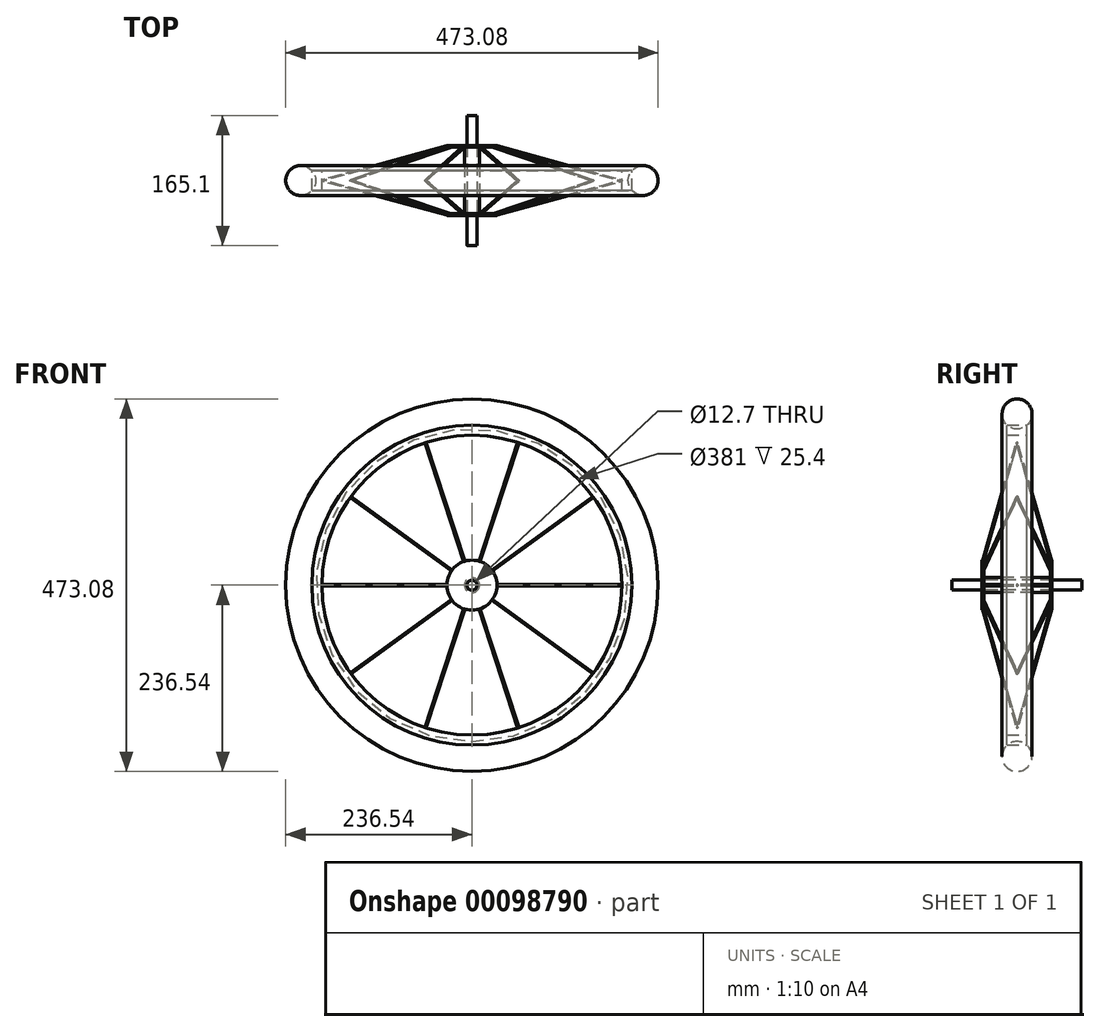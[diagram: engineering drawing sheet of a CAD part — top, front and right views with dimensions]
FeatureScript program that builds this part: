
annotation { "Feature Type Name" : "Feature", "Feature Type Description" : "" }
export const myFeature = defineFeature(function(context is Context, id is Id, definition is map)
    precondition{}
    {
        {
            var Q0;
            Q0=qCreatedBy(makeId("Front.planeOp"),FACE);
            var sketch = newSketch(context, id + "F0", { "sketchPlane" : qUnion([Q0])});
            skCircle(sketch, "E0", {"center": v(0, 0) * mm, "radius": 203.2 * mm});
            skCircle(sketch, "E1", {"center": v(0, 0) * mm, "radius": 190.5 * mm});
            skCircle(sketch, "E2.cCircle", {"center": v(0, 0) * mm, "radius": 163.56 * mm, "construction": true});
            skLineSegment(sketch, "E2.0", {"start": v(163.56, 43.83) * mm, "end": v(163.56, -43.83) * mm});
            skLineSegment(sketch, "E2.1", {"start": v(163.56, -43.83) * mm, "end": v(119.74, -119.74) * mm});
            skLineSegment(sketch, "E2.2", {"start": v(119.74, -119.74) * mm, "end": v(43.83, -163.56) * mm});
            skLineSegment(sketch, "E2.3", {"start": v(43.83, -163.56) * mm, "end": v(-43.83, -163.56) * mm});
            skLineSegment(sketch, "E2.4", {"start": v(-43.83, -163.56) * mm, "end": v(-119.74, -119.74) * mm});
            skLineSegment(sketch, "E2.5", {"start": v(-119.74, -119.74) * mm, "end": v(-163.56, -43.83) * mm});
            skLineSegment(sketch, "E2.6", {"start": v(-163.56, -43.83) * mm, "end": v(-163.56, 43.83) * mm});
            skLineSegment(sketch, "E2.7", {"start": v(-163.56, 43.83) * mm, "end": v(-119.74, 119.74) * mm});
            skLineSegment(sketch, "E2.8", {"start": v(-119.74, 119.74) * mm, "end": v(-43.83, 163.56) * mm});
            skLineSegment(sketch, "E2.9", {"start": v(-43.83, 163.56) * mm, "end": v(43.83, 163.56) * mm});
            skLineSegment(sketch, "E2.10", {"start": v(43.83, 163.56) * mm, "end": v(119.74, 119.74) * mm});
            skLineSegment(sketch, "E2.11", {"start": v(119.74, 119.74) * mm, "end": v(163.56, 43.83) * mm});
            skPoint(sketch, "E2.0.midPoint", {"position": v(163.56, 0) * mm});
            skLineSegment(sketch, "E3", {"start": v(163.56, 43.83) * mm, "end": v(-163.56, -43.83) * mm});
            skLineSegment(sketch, "E4", {"start": v(119.74, -119.74) * mm, "end": v(-119.74, 119.74) * mm});
            skLineSegment(sketch, "E5", {"start": v(-43.83, -163.56) * mm, "end": v(43.83, 163.56) * mm});
            skLineSegment(sketch, "E6", {"start": v(-119.74, -119.74) * mm, "end": v(119.74, 119.74) * mm});
            skLineSegment(sketch, "E7", {"start": v(43.83, -163.56) * mm, "end": v(-43.83, 163.56) * mm});
            skLineSegment(sketch, "E8", {"start": v(163.56, -43.83) * mm, "end": v(-163.56, 43.83) * mm});
            skSolve(sketch);
        }
        {
            var Q0;
            Q0 = qSketchRegion(id + "F0", true);
            extrude(context, id + "F1", {"entities" : qUnion([Q0]), "depth" : 25.4 * mm, "symmetric" : true});
        }
        {
            var Q0;
            Q0=qCreatedBy(makeId("Right.planeOp"),FACE);
            var sketch = newSketch(context, id + "F2", { "sketchPlane" : qUnion([Q0])});
            skLineSegment(sketch, "E9", {"start": v(-44.45, 6.35) * mm, "end": v(-44.45, 31.75) * mm});
            skLineSegment(sketch, "E10", {"start": v(-44.45, 31.75) * mm, "end": v(-42.16, 31.75) * mm});
            skLineSegment(sketch, "E11", {"start": v(-42.16, 31.75) * mm, "end": v(-42.16, 9.53) * mm});
            skLineSegment(sketch, "E12", {"start": v(-44.45, 6.35) * mm, "end": v(44.45, 6.35) * mm});
            skLineSegment(sketch, "E13", {"start": v(42.16, 9.53) * mm, "end": v(42.16, 31.75) * mm});
            skLineSegment(sketch, "E14", {"start": v(42.16, 31.75) * mm, "end": v(44.45, 31.75) * mm});
            skLineSegment(sketch, "E15", {"start": v(44.45, 31.75) * mm, "end": v(44.45, 6.35) * mm});
            skPoint(sketch, "E16.orphan", {"position": v(-44.45, 0) * mm});
            skPoint(sketch, "E17.orphan", {"position": v(44.45, 0) * mm});
            skLineSegment(sketch, "E18.trimOffspring", {"start": v(-42.16, 9.53) * mm, "end": v(42.16, 9.53) * mm});
            skSolve(sketch);
        }
        {
            var Q0;
            Q0=makeQuery(id+"F2.imprint","IMPRINT",FACE,{"disambiguationData":[TD([[makeQuery(id+"F2.imprint","IMPRINT",EDGE,{"derivedFrom":sQuery(id+"F2.wireOp",EDGE,"E9")}),-1.0]])]});
            var Q1;
            Q1=makeQuery(id+"F1.opExtrude","CAP_EDGE",EDGE,{"disambiguationData":[OSD([sQuery(id+"F0.wireOp",EDGE,"E1")])],"isStart":false});
            sweep(context, id + "F3", {"profiles" : qUnion([Q0]), "path" : qUnion([Q1])});
        }
        {
            var Q0;
            Q0=qCreatedBy(makeId("Top.planeOp"),FACE);
            var sketch = newSketch(context, id + "F4", { "sketchPlane" : qUnion([Q0])});
            skLineSegment(sketch, "E19", {"start": v(31.75, 42.5) * mm, "end": v(190.5, -0.76) * mm});
            skLineSegment(sketch, "E20", {"start": v(31.75, 44.09) * mm, "end": v(190.5, 0.82) * mm});
            skLineSegment(sketch, "E21", {"start": v(31.75, 42.5) * mm, "end": v(31.75, 44.09) * mm});
            skLineSegment(sketch, "E22", {"start": v(190.5, -0.76) * mm, "end": v(190.5, 0.82) * mm});
            skSolve(sketch);
        }
        {
            var Q0;
            Q0=makeQuery(id+"F4.imprint","IMPRINT",FACE,{"disambiguationData":[TD([[makeQuery(id+"F4.imprint","IMPRINT",EDGE,{"derivedFrom":sQuery(id+"F4.wireOp",EDGE,"E19")}),1.0]])]});
            extrude(context, id + "F5", {"entities" : qUnion([Q0]), "depth" : 1.52 * mm, "symmetric" : true});
        }
        {
            var Q0;
            Q0=qCreatedBy(makeId("Front.planeOp"),FACE);
            var sketch = newSketch(context, id + "F6", { "sketchPlane" : qUnion([Q0])});
            skPoint(sketch, "E23.0.midPoint", {"position": v(0, 148.93) * mm});
            skLineSegment(sketch, "E24", {"start": v(0, 0) * mm, "end": v(126.69, 92.05) * mm});
            skLineSegment(sketch, "E25", {"start": v(0, 0) * mm, "end": v(48.4, 148.93) * mm});
            skLineSegment(sketch, "E26", {"start": v(0, 0) * mm, "end": v(-48.4, 148.93) * mm});
            skLineSegment(sketch, "E27", {"start": v(0, 0) * mm, "end": v(-126.69, 92.05) * mm});
            skSolve(sketch);
        }
        {
            var Q0;
            Q0=sQuery(id+"F6.wireOp",EDGE,"E24");
            cPlane(context, id + "F7", {"entities" : qUnion([Q0]), "cplaneType" : CPlaneType.LINE_ANGLE, "offset" : 152.4 * mm, "angle" : 90 * degree, "width" : 152.4 * mm, "height" : 152.4 * mm});
        }
        {
            var Q0;
            Q0=sQuery(id+"F6.wireOp",EDGE,"E25");
            cPlane(context, id + "F8", {"entities" : qUnion([Q0]), "cplaneType" : CPlaneType.LINE_ANGLE, "offset" : 152.4 * mm, "angle" : 0 * degree, "width" : 152.4 * mm, "height" : 152.4 * mm});
        }
        {
            var Q0;
            Q0=sQuery(id+"F6.wireOp",EDGE,"E27");
            cPlane(context, id + "F9", {"entities" : qUnion([Q0]), "cplaneType" : CPlaneType.LINE_ANGLE, "offset" : 152.4 * mm, "angle" : 90 * degree, "width" : 152.4 * mm, "height" : 152.4 * mm});
        }
        {
            var Q0;
            Q0=makeQuery(id+"F5.opExtrude","SWEPT_BODY",BODY,{"disambiguationData":[OSD([sQuery(id+"F4.wireOp",EDGE,"E19"),sQuery(id+"F4.wireOp",EDGE,"E20"),sQuery(id+"F4.wireOp",EDGE,"E21"),sQuery(id+"F4.wireOp",EDGE,"E22")])]});
            var Q1;
            Q1=qCreatedBy(id+"F7.planeOp",FACE);
            mirror(context, id + "F10", {"entities" : qUnion([Q0]), "mirrorPlane" : qUnion([Q1])});
        }
        {
            var Q0;
            Q0=makeQuery(id+"F10.opPattern","COPY",BODY,{"derivedFrom":makeQuery(id+"F5.opExtrude","SWEPT_BODY",BODY,{"disambiguationData":[OSD([sQuery(id+"F4.wireOp",EDGE,"E19"),sQuery(id+"F4.wireOp",EDGE,"E20"),sQuery(id+"F4.wireOp",EDGE,"E21"),sQuery(id+"F4.wireOp",EDGE,"E22")])]}),"instanceName":"1"});
            var Q1;
            Q1=qCreatedBy(id+"F9.planeOp",FACE);
            mirror(context, id + "F11", {"entities" : qUnion([Q0]), "mirrorPlane" : qUnion([Q1])});
        }
        {
            var Q0;
            Q0=makeQuery(id+"F5.opExtrude","SWEPT_BODY",BODY,{"disambiguationData":[OSD([sQuery(id+"F4.wireOp",EDGE,"E19"),sQuery(id+"F4.wireOp",EDGE,"E20"),sQuery(id+"F4.wireOp",EDGE,"E21"),sQuery(id+"F4.wireOp",EDGE,"E22")])]});
            var Q1;
            Q1=qCreatedBy(id+"F8.planeOp",FACE);
            mirror(context, id + "F12", {"entities" : qUnion([Q0]), "mirrorPlane" : qUnion([Q1])});
        }
        {
            var Q0;
            Q0=makeQuery(id+"F5.opExtrude","SWEPT_BODY",BODY,{"disambiguationData":[OSD([sQuery(id+"F4.wireOp",EDGE,"E19"),sQuery(id+"F4.wireOp",EDGE,"E20"),sQuery(id+"F4.wireOp",EDGE,"E21"),sQuery(id+"F4.wireOp",EDGE,"E22")])]});
            var Q1;
            Q1=qCreatedBy(makeId("Right.planeOp"),FACE);
            mirror(context, id + "F13", {"entities" : qUnion([Q0]), "mirrorPlane" : qUnion([Q1])});
        }
        {
            var Q0;
            Q0=makeQuery(id+"F13.opPattern","COPY",BODY,{"derivedFrom":makeQuery(id+"F5.opExtrude","SWEPT_BODY",BODY,{"disambiguationData":[OSD([sQuery(id+"F4.wireOp",EDGE,"E19"),sQuery(id+"F4.wireOp",EDGE,"E20"),sQuery(id+"F4.wireOp",EDGE,"E21"),sQuery(id+"F4.wireOp",EDGE,"E22")])]}),"instanceName":"1"});
            var Q1;
            Q1=qCreatedBy(id+"F9.planeOp",FACE);
            mirror(context, id + "F14", {"entities" : qUnion([Q0]), "mirrorPlane" : qUnion([Q1])});
        }
        {
            var Q0;
            Q0=makeQuery(id+"F14.opPattern","COPY",BODY,{"derivedFrom":makeQuery(id+"F13.opPattern","COPY",BODY,{"derivedFrom":makeQuery(id+"F5.opExtrude","SWEPT_BODY",BODY,{"disambiguationData":[OSD([sQuery(id+"F4.wireOp",EDGE,"E19"),sQuery(id+"F4.wireOp",EDGE,"E20"),sQuery(id+"F4.wireOp",EDGE,"E21"),sQuery(id+"F4.wireOp",EDGE,"E22")])]}),"instanceName":"1"}),"instanceName":"1"});
            var Q1;
            Q1=qCreatedBy(id+"F8.planeOp",FACE);
            mirror(context, id + "F15", {"entities" : qUnion([Q0]), "mirrorPlane" : qUnion([Q1])});
        }
        {
            var Q0;
            Q0=makeQuery(id+"F14.opPattern","COPY",BODY,{"derivedFrom":makeQuery(id+"F13.opPattern","COPY",BODY,{"derivedFrom":makeQuery(id+"F5.opExtrude","SWEPT_BODY",BODY,{"disambiguationData":[OSD([sQuery(id+"F4.wireOp",EDGE,"E19"),sQuery(id+"F4.wireOp",EDGE,"E20"),sQuery(id+"F4.wireOp",EDGE,"E21"),sQuery(id+"F4.wireOp",EDGE,"E22")])]}),"instanceName":"1"}),"instanceName":"1"});
            var Q1;
            Q1=makeQuery(id+"F10.opPattern","COPY",BODY,{"derivedFrom":makeQuery(id+"F5.opExtrude","SWEPT_BODY",BODY,{"disambiguationData":[OSD([sQuery(id+"F4.wireOp",EDGE,"E19"),sQuery(id+"F4.wireOp",EDGE,"E20"),sQuery(id+"F4.wireOp",EDGE,"E21"),sQuery(id+"F4.wireOp",EDGE,"E22")])]}),"instanceName":"1"});
            var Q2;
            Q2=makeQuery(id+"F15.opPattern","COPY",BODY,{"derivedFrom":makeQuery(id+"F14.opPattern","COPY",BODY,{"derivedFrom":makeQuery(id+"F13.opPattern","COPY",BODY,{"derivedFrom":makeQuery(id+"F5.opExtrude","SWEPT_BODY",BODY,{"disambiguationData":[OSD([sQuery(id+"F4.wireOp",EDGE,"E19"),sQuery(id+"F4.wireOp",EDGE,"E20"),sQuery(id+"F4.wireOp",EDGE,"E21"),sQuery(id+"F4.wireOp",EDGE,"E22")])]}),"instanceName":"1"}),"instanceName":"1"}),"instanceName":"1"});
            var Q3;
            Q3=qCreatedBy(makeId("Top.planeOp"),FACE);
            mirror(context, id + "F16", {"entities" : qUnion([Q0, Q1, Q2]), "mirrorPlane" : qUnion([Q3])});
        }
        {
            var Q0;
            Q0=makeQuery(id+"F10.opPattern","COPY",BODY,{"derivedFrom":makeQuery(id+"F5.opExtrude","SWEPT_BODY",BODY,{"disambiguationData":[OSD([sQuery(id+"F4.wireOp",EDGE,"E19"),sQuery(id+"F4.wireOp",EDGE,"E20"),sQuery(id+"F4.wireOp",EDGE,"E21"),sQuery(id+"F4.wireOp",EDGE,"E22")])]}),"instanceName":"1"});
            var Q1;
            Q1=makeQuery(id+"F14.opPattern","COPY",BODY,{"derivedFrom":makeQuery(id+"F13.opPattern","COPY",BODY,{"derivedFrom":makeQuery(id+"F5.opExtrude","SWEPT_BODY",BODY,{"disambiguationData":[OSD([sQuery(id+"F4.wireOp",EDGE,"E19"),sQuery(id+"F4.wireOp",EDGE,"E20"),sQuery(id+"F4.wireOp",EDGE,"E21"),sQuery(id+"F4.wireOp",EDGE,"E22")])]}),"instanceName":"1"}),"instanceName":"1"});
            var Q2;
            Q2=makeQuery(id+"F12.opPattern","COPY",BODY,{"derivedFrom":makeQuery(id+"F5.opExtrude","SWEPT_BODY",BODY,{"disambiguationData":[OSD([sQuery(id+"F4.wireOp",EDGE,"E19"),sQuery(id+"F4.wireOp",EDGE,"E20"),sQuery(id+"F4.wireOp",EDGE,"E21"),sQuery(id+"F4.wireOp",EDGE,"E22")])]}),"instanceName":"1"});
            var Q3;
            Q3=makeQuery(id+"F13.opPattern","COPY",BODY,{"derivedFrom":makeQuery(id+"F5.opExtrude","SWEPT_BODY",BODY,{"disambiguationData":[OSD([sQuery(id+"F4.wireOp",EDGE,"E19"),sQuery(id+"F4.wireOp",EDGE,"E20"),sQuery(id+"F4.wireOp",EDGE,"E21"),sQuery(id+"F4.wireOp",EDGE,"E22")])]}),"instanceName":"1"});
            var Q4;
            Q4=makeQuery(id+"F11.opPattern","COPY",BODY,{"derivedFrom":makeQuery(id+"F10.opPattern","COPY",BODY,{"derivedFrom":makeQuery(id+"F5.opExtrude","SWEPT_BODY",BODY,{"disambiguationData":[OSD([sQuery(id+"F4.wireOp",EDGE,"E19"),sQuery(id+"F4.wireOp",EDGE,"E20"),sQuery(id+"F4.wireOp",EDGE,"E21"),sQuery(id+"F4.wireOp",EDGE,"E22")])]}),"instanceName":"1"}),"instanceName":"1"});
            var Q5;
            Q5=makeQuery(id+"F16.opPattern","COPY",BODY,{"derivedFrom":makeQuery(id+"F14.opPattern","COPY",BODY,{"derivedFrom":makeQuery(id+"F13.opPattern","COPY",BODY,{"derivedFrom":makeQuery(id+"F5.opExtrude","SWEPT_BODY",BODY,{"disambiguationData":[OSD([sQuery(id+"F4.wireOp",EDGE,"E19"),sQuery(id+"F4.wireOp",EDGE,"E20"),sQuery(id+"F4.wireOp",EDGE,"E21"),sQuery(id+"F4.wireOp",EDGE,"E22")])]}),"instanceName":"1"}),"instanceName":"1"}),"instanceName":"1"});
            var Q6;
            Q6=makeQuery(id+"F16.opPattern","COPY",BODY,{"derivedFrom":makeQuery(id+"F10.opPattern","COPY",BODY,{"derivedFrom":makeQuery(id+"F5.opExtrude","SWEPT_BODY",BODY,{"disambiguationData":[OSD([sQuery(id+"F4.wireOp",EDGE,"E19"),sQuery(id+"F4.wireOp",EDGE,"E20"),sQuery(id+"F4.wireOp",EDGE,"E21"),sQuery(id+"F4.wireOp",EDGE,"E22")])]}),"instanceName":"1"}),"instanceName":"1"});
            var Q7;
            Q7=makeQuery(id+"F16.opPattern","COPY",BODY,{"derivedFrom":makeQuery(id+"F15.opPattern","COPY",BODY,{"derivedFrom":makeQuery(id+"F14.opPattern","COPY",BODY,{"derivedFrom":makeQuery(id+"F13.opPattern","COPY",BODY,{"derivedFrom":makeQuery(id+"F5.opExtrude","SWEPT_BODY",BODY,{"disambiguationData":[OSD([sQuery(id+"F4.wireOp",EDGE,"E19"),sQuery(id+"F4.wireOp",EDGE,"E20"),sQuery(id+"F4.wireOp",EDGE,"E21"),sQuery(id+"F4.wireOp",EDGE,"E22")])]}),"instanceName":"1"}),"instanceName":"1"}),"instanceName":"1"}),"instanceName":"1"});
            var Q8;
            Q8=makeQuery(id+"F5.opExtrude","SWEPT_BODY",BODY,{"disambiguationData":[OSD([sQuery(id+"F4.wireOp",EDGE,"E19"),sQuery(id+"F4.wireOp",EDGE,"E20"),sQuery(id+"F4.wireOp",EDGE,"E21"),sQuery(id+"F4.wireOp",EDGE,"E22")])]});
            var Q9;
            Q9=makeQuery(id+"F15.opPattern","COPY",BODY,{"derivedFrom":makeQuery(id+"F14.opPattern","COPY",BODY,{"derivedFrom":makeQuery(id+"F13.opPattern","COPY",BODY,{"derivedFrom":makeQuery(id+"F5.opExtrude","SWEPT_BODY",BODY,{"disambiguationData":[OSD([sQuery(id+"F4.wireOp",EDGE,"E19"),sQuery(id+"F4.wireOp",EDGE,"E20"),sQuery(id+"F4.wireOp",EDGE,"E21"),sQuery(id+"F4.wireOp",EDGE,"E22")])]}),"instanceName":"1"}),"instanceName":"1"}),"instanceName":"1"});
            var Q10;
            Q10=qCreatedBy(makeId("Front.planeOp"),FACE);
            mirror(context, id + "F17", {"entities" : qUnion([Q0, Q1, Q2, Q3, Q4, Q5, Q6, Q7, Q8, Q9]), "mirrorPlane" : qUnion([Q10])});
        }
        {
            var Q0;
            Q0=makeQuery(id+"F3.opSweep","SWEPT_FACE",FACE,{"disambiguationData":[OSD([sQuery(id+"F0.wireOp",EDGE,"E1"),sQuery(id+"F2.wireOp",EDGE,"E15")])]});
            var sketch = newSketch(context, id + "F18", { "sketchPlane" : qUnion([Q0])});
            skCircle(sketch, "E28", {"center": v(0, 0) * mm, "radius": 6.35 * mm});
            skSolve(sketch);
        }
        {
            var Q0;
            Q0 = qSketchRegion(id + "F18", true);
            extrude(context, id + "F19", {"entities" : qUnion([Q0]), "oppositeDirection" : true, "depth" : 127 * mm, "hasSecondDirection" : true, "secondDirectionOppositeDirection" : false, "secondDirectionDepth" : 38.1 * mm});
        }
        {
            var Q0;
            Q0=qCreatedBy(makeId("Right.planeOp"),FACE);
            var sketch = newSketch(context, id + "F20", { "sketchPlane" : qUnion([Q0])});
            skCircle(sketch, "E29", {"center": v(0, 217.49) * mm, "radius": 19.05 * mm});
            skSolve(sketch);
        }
        {
            var Q0;
            Q0=makeQuery(id+"F20.imprint","IMPRINT",FACE,{"disambiguationData":[TD([[makeQuery(id+"F20.imprint","IMPRINT",EDGE,{"derivedFrom":sQuery(id+"F20.wireOp",EDGE,"E29")}),1.0]])]});
            var Q1;
            Q1=makeQuery(id+"F1.opExtrude","CAP_EDGE",EDGE,{"disambiguationData":[OSD([sQuery(id+"F0.wireOp",EDGE,"E0")])],"isStart":true});
            sweep(context, id + "F21", {"profiles" : qUnion([Q0]), "path" : qUnion([Q1])});
        }
    });
